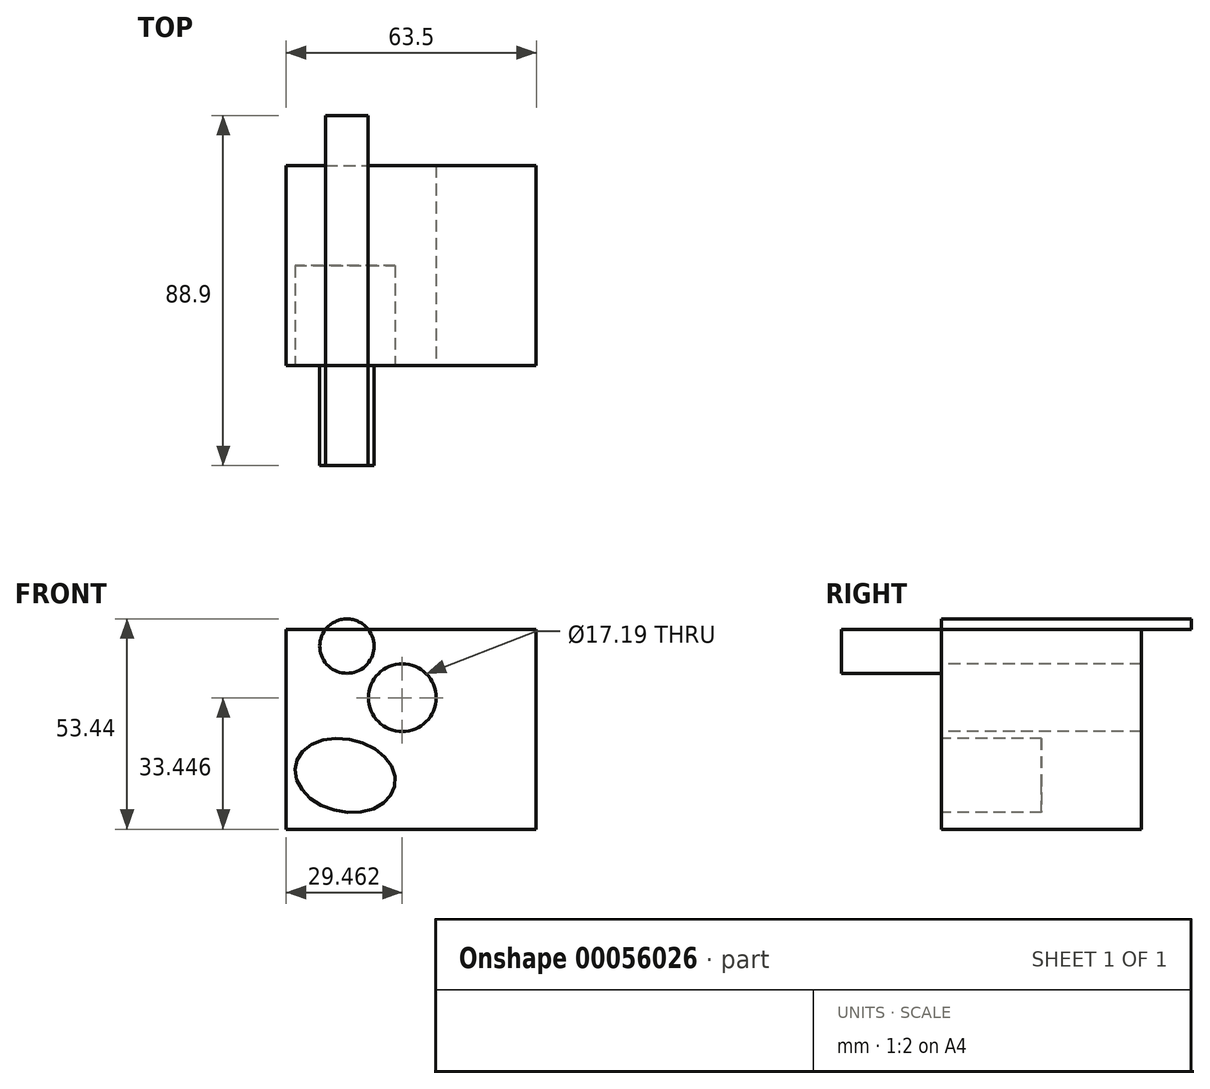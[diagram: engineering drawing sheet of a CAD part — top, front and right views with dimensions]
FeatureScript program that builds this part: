
annotation { "Feature Type Name" : "Feature", "Feature Type Description" : "" }
export const myFeature = defineFeature(function(context is Context, id is Id, definition is map)
    precondition{}
    {
        {
            var Q0;
            Q0=qCreatedBy(makeId("Front.planeOp"),FACE);
            var sketch = newSketch(context, id + "F0", { "sketchPlane" : qUnion([Q0])});
            skLineSegment(sketch, "E0.bottom", {"start": v(-51.78, 63.37) * mm, "end": v(11.72, 63.37) * mm});
            skLineSegment(sketch, "E0.top", {"start": v(-51.78, 12.57) * mm, "end": v(11.72, 12.57) * mm});
            skLineSegment(sketch, "E0.left", {"start": v(-51.78, 63.37) * mm, "end": v(-51.78, 12.57) * mm});
            skLineSegment(sketch, "E0.right", {"start": v(11.72, 63.37) * mm, "end": v(11.72, 12.57) * mm});
            skSolve(sketch);
        }
        {
            var Q0;
            Q0 = qSketchRegion(id + "F0", true);
            extrude(context, id + "F1", {"entities" : qUnion([Q0]), "depth" : 50.8 * mm});
        }
        {
            var Q0;
            Q0=makeQuery(id+"F1.opExtrude","CAP_FACE",FACE,{"disambiguationData":[OSD([sQuery(id+"F0.wireOp",EDGE,"E0.bottom"),sQuery(id+"F0.wireOp",EDGE,"E0.top"),sQuery(id+"F0.wireOp",EDGE,"E0.left"),sQuery(id+"F0.wireOp",EDGE,"E0.right")])],"isStart":false});
            var sketch = newSketch(context, id + "F2", { "sketchPlane" : qUnion([Q0])});
            skCircle(sketch, "E1", {"center": v(-36.38, 59.1) * mm, "radius": 6.9 * mm});
            skPoint(sketch, "E1.first.point", {"position": v(-39.8, 53.12) * mm});
            skPoint(sketch, "E1.second.point", {"position": v(-43.2, 60.13) * mm});
            skPoint(sketch, "E1.third.point", {"position": v(-29.58, 58) * mm});
            skCircle(sketch, "E2", {"center": v(-22.32, 46.02) * mm, "radius": 8.6 * mm});
            skEllipse(sketch, "E3", {"center": v(-36.84, 26.27) * mm, "majorRadius": 12.88 * mm, "minorRadius": 9.24 * mm, "majorAxis": v(0.98, -0.21)});
            skSolve(sketch);
        }
        {
            var Q0;
            {var subQ0=sQuery(id+"F2.wireOp",EDGE,"E1");var subQ1=makeQuery(id+"F1.opExtrude","CAP_EDGE",EDGE,{"disambiguationData":[OSD([sQuery(id+"F0.wireOp",EDGE,"E0.bottom")])],"isStart":false});var subQ2=makeQuery(id+"F2.imprint","INTERSECT",VERTEX,{"disambiguationData":[OD(0.0)],"derivedFrom":[subQ1,subQ0]});Q0=makeQuery(id+"F2.imprint","IMPRINT",FACE,{"disambiguationData":[TD([[makeQuery(id+"F2.imprint","IMPRINT",EDGE,{"disambiguationData":[TD([[subQ2,-1.0]])],"derivedFrom":subQ0}),1.0]])]});}
            extrude(context, id + "F3", {"entities" : qUnion([Q0]), "operationType" : NewBodyOperationType.ADD, "depth" : 25.4 * mm});
        }
        {
            var Q0;
            Q0=makeQuery(id+"F2.imprint","IMPRINT",FACE,{"disambiguationData":[TD([[makeQuery(id+"F2.imprint","IMPRINT",EDGE,{"derivedFrom":sQuery(id+"F2.wireOp",EDGE,"E2")}),1.0]])]});
            extrude(context, id + "F4", {"entities" : qUnion([Q0]), "operationType" : NewBodyOperationType.REMOVE, "oppositeDirection" : true, "depth" : 50.8 * mm});
        }
        {
            var Q0;
            Q0=makeQuery(id+"F2.imprint","IMPRINT",FACE,{"disambiguationData":[TD([[makeQuery(id+"F2.imprint","IMPRINT",EDGE,{"derivedFrom":sQuery(id+"F2.wireOp",EDGE,"E3")}),1.0]])]});
            extrude(context, id + "F5", {"entities" : qUnion([Q0]), "operationType" : NewBodyOperationType.REMOVE, "oppositeDirection" : true, "depth" : 25.4 * mm});
        }
        {
            var Q0;
            {var subQ0=sQuery(id+"F2.wireOp",EDGE,"E1");var subQ1=makeQuery(id+"F1.opExtrude","CAP_EDGE",EDGE,{"disambiguationData":[OSD([sQuery(id+"F0.wireOp",EDGE,"E0.bottom")])],"isStart":false});var subQ2=makeQuery(id+"F2.imprint","INTERSECT",VERTEX,{"disambiguationData":[OD(0.0)],"derivedFrom":[subQ1,subQ0]});Q0=makeQuery(id+"F2.imprint","IMPRINT",FACE,{"disambiguationData":[TD([[makeQuery(id+"F2.imprint","IMPRINT",EDGE,{"disambiguationData":[TD([[subQ2,1.0]])],"derivedFrom":subQ0}),1.0]])]});}
            extrude(context, id + "F6", {"entities" : qUnion([Q0]), "operationType" : NewBodyOperationType.ADD, "oppositeDirection" : true, "depth" : 63.5 * mm});
        }
    });
